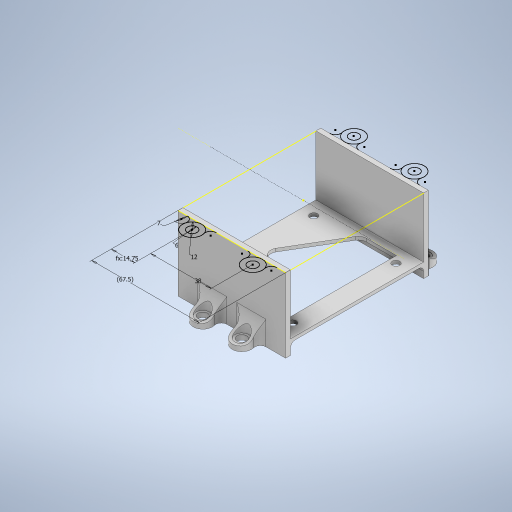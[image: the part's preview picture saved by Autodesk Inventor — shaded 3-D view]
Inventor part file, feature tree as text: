
AUTODESK INVENTOR PART (.ipt)
format: ipt  version: 2024 (Build 280153000, 153)  size: 491,520 bytes
history: native  units: in
note: dims shown in document units (in); Inventor stores cm internally (conversion verified against a paired STEP export)
features: extrude x6, fillet x2, plane x1, sketch x1
ambient origin geometry x8: Origin, YZ Plane, XZ Plane, XY Plane, X Axis, Y Axis, Z Axis, Center Point
bodies: Solid1 (feature_tree)
feature tree (10):
  extrude  "Extrusion1"  Depth=0.1181in
  extrude  "Extrusion2"  Depth=0.1181in
  extrude  "Extrusion6"  Depth=0.1969in
  extrude  "Extrusion7"  Depth=0.1969in
  extrude  "Extrusion8"  Depth=0.4724in
  plane  "Work Plane1"
  extrude  "Extrusion9"  Depth=0.4724in
  fillet  "Fillet2"  Radius=2.6575in
  fillet  "Fillet7"  Radius=1.3287in
  sketch  "Sketch9"  dims[d0=3.2874in d1=0.1181in d2=0.1181in d4=0.1969in d5=0.1969in d6=0.4724in d7=0.4724in d8=2.6575in d9=1.3287in d10=1.6437in d11=0.0787in d12=0.0in d13=1.5551in d14=0.2756in d15=0.0in d16=0.0in d35=0.185in d36=0.313in d38=0.313in d40=0.1181in d41=0.0in d46=0.2362in d47=0.2362in d48=0.2362in d49=0.2362in d51=0.4724in d54=0.1378in d55=0.9646in d56=1.9291in d57=0.4823in d58=0.9646in d59=0.5906in d60=0.0in d61=0.3346in d62=0.3346in d63=0.3346in d64=0.3346in d65=0.4724in d66=0.0in d67=1.1811in d68=0.1181in d69=0.1969in d70=0.0in d72=0.3346in d73=2.5512in d74=1.2756in d75=2.7559in d76=0.0in d77=0.1969in d80=0.1181in d85=0.1181in d87=0.0662in d90=0.2362in d91=0.4724in d92=0.2756in d93=1.4961in d94=2.6575in d95=0.5807in d31=0.0197in d32=0.0344in d33=0.0197in d34=0.0344in]
